# Revit family: LAMP_MOODY RFL. ROUND 072 FIX
name_source: partatom
category: Modelos genéricos
revit_build: Autodesk Revit 2015 (Build: 20140606_1530(x64)
units: mm (PartAtom-declared; Revit-internal decimal feet)

## types (4) — shared parameters
Accessory Type = Assembly
Diameter = 72 mm  [stored 0.23622 ft]
Fabricante = LAMP
Last update = 29/08/2019
Manufacturer URL = http://www.lamp.es
Manufacturer country = Spain
Manufacturer name = LAMP
Material Muelle Emp. = LAMP_Acero genérico
Product URL = https://www.lamp.es
Product datasheet = https://www.lamp.es
Recessed diameter = 68 mm
Weight = 0.03 kg

## per-type parameters (varying)
| type | Descripción | Finish | Material Reflector | Modelo | Product code |
| COPPER FINISH | MOODY ACC. RFL. ROUND 072 FIX CO. | Metalized matt copper | LAMP_PC Reflector Moody CO | MORFRD072FXC | MORFRD072FXC |
| WHITE FINISH | MOODY ACC. RFL. ROUND 072 FIX WH. | Matt white | LAMP_PC Reflector Moody BL | MORFRD072FXW | MORFRD072FXW |
| SILVER FINISH | MOODY ACC. RFL. ROUND 072 FIX MET. | Metalized matt silver | LAMP_PC Reflector Moody GR | MORFRD072FXM | MORFRD072FXM |
| BLACK FINISH | MOODY ACC. RFL. ROUND 072 FIX BK. | Matt black | LAMP_PC Reflector Moody NG | MORFRD072FXB | MORFRD072FXB |

note: [stored X ft] marks values corroborated as IEEE doubles in the binary element streams (Revit-internal decimal feet)
